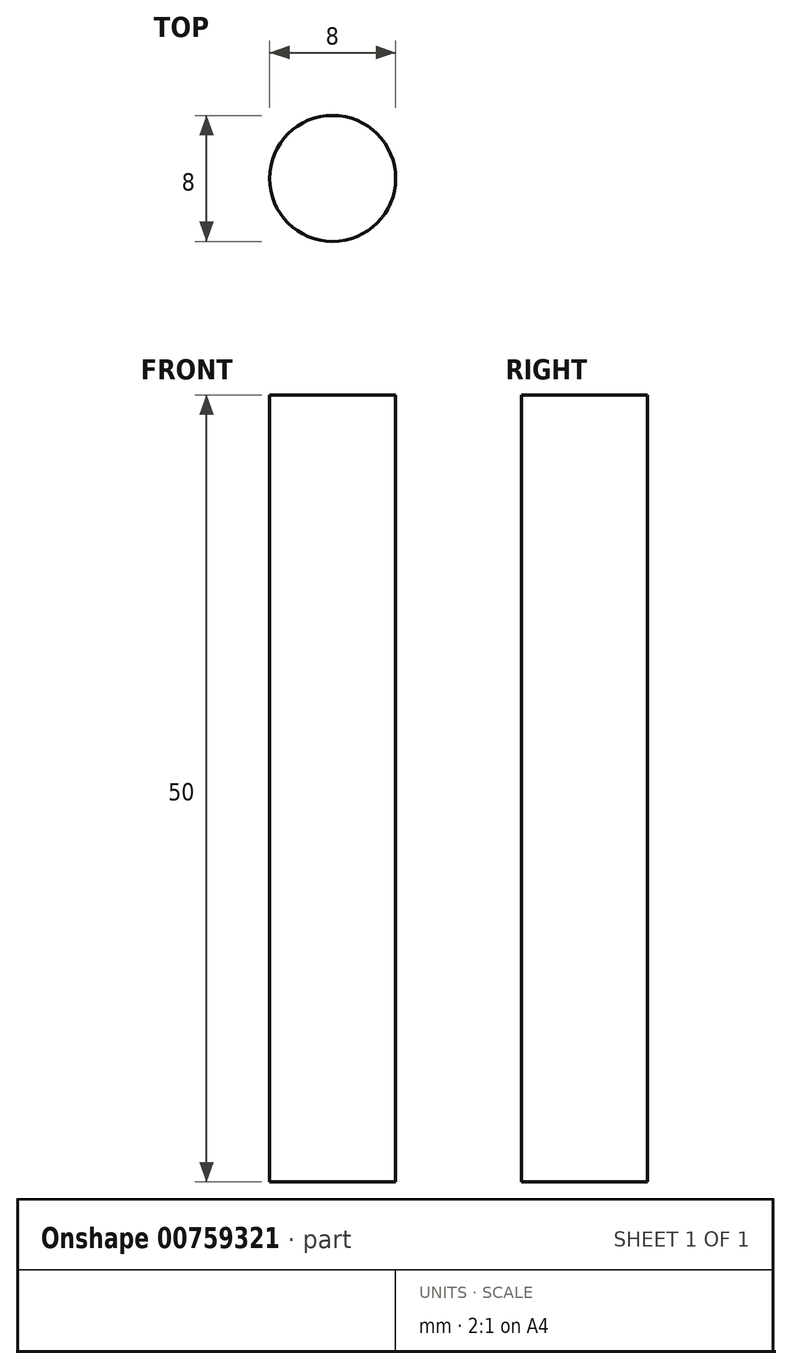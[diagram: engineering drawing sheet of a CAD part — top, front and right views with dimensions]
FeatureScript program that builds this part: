
annotation { "Feature Type Name" : "Feature", "Feature Type Description" : "" }
export const myFeature = defineFeature(function(context is Context, id is Id, definition is map)
    precondition{}
    {
        {
            var Q0;
            Q0=qCreatedBy(makeId("Top.planeOp"),FACE);
            var sketch = newSketch(context, id + "F0", { "sketchPlane" : qUnion([Q0])});
            skCircle(sketch, "E0", {"center": v(0, 0) * mm, "radius": 4 * mm});
            skSolve(sketch);
        }
        {
            var Q0;
            Q0=makeQuery(id+"F0.imprint","IMPRINT",FACE,{"disambiguationData":[TD([[makeQuery(id+"F0.imprint","IMPRINT",EDGE,{"derivedFrom":sQuery(id+"F0.wireOp",EDGE,"E0")}),1.0]])]});
            extrude(context, id + "F1", {"entities" : qUnion([Q0]), "depth" : 50 * mm, "offsetDistance" : 25 * mm});
        }
    });
